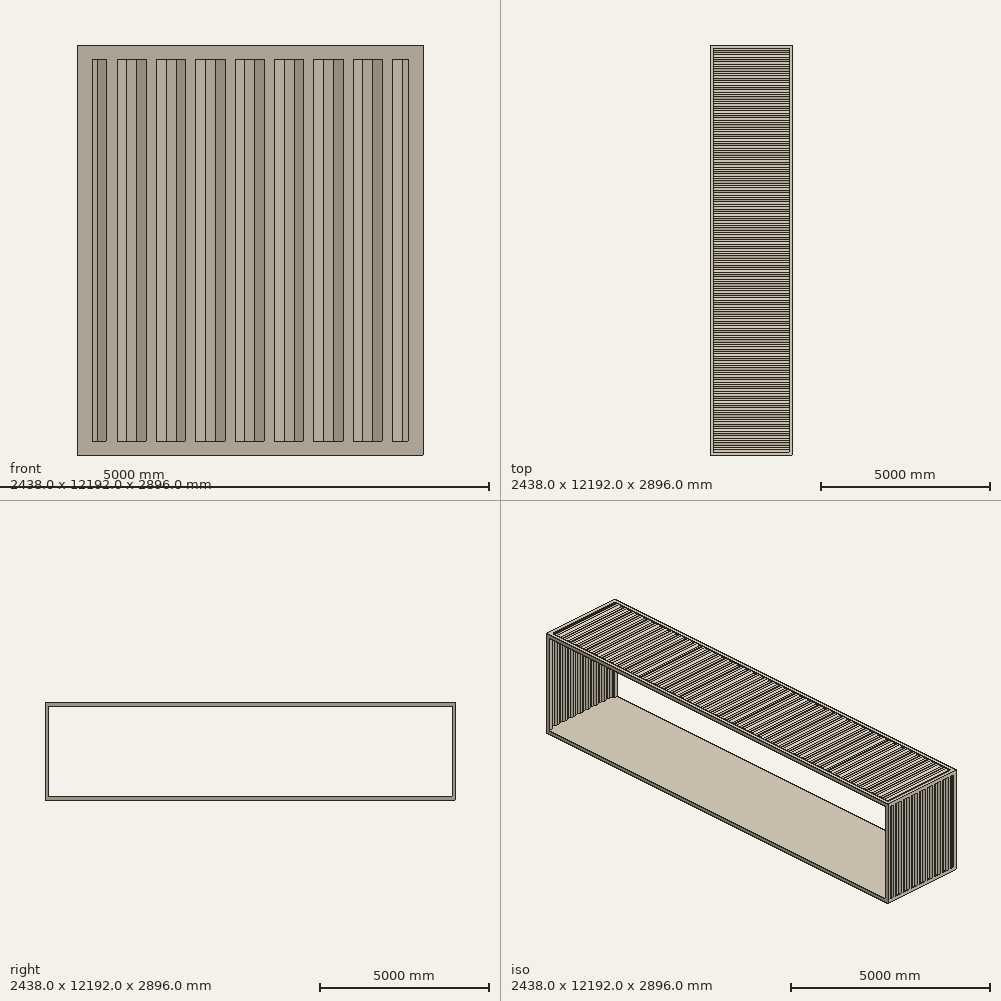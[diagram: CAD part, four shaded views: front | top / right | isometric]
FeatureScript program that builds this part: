
annotation { "Feature Type Name" : "Feature", "Feature Type Description" : "" }
export const myFeature = defineFeature(function(context is Context, id is Id, definition is map)
    precondition{}
    {
        {
            var Q0;
            Q0=qCreatedBy(makeId("Top.planeOp"),FACE);
            var sketch = newSketch(context, id + "F0", { "sketchPlane" : qUnion([Q0])});
            skLineSegment(sketch, "E0.bottom", {"start": v(0, 0) * mm, "end": v(-2438, 0) * mm});
            skLineSegment(sketch, "E0.top", {"start": v(0, 12192) * mm, "end": v(-2438, 12192) * mm});
            skLineSegment(sketch, "E0.left", {"start": v(0, 0) * mm, "end": v(0, 12192) * mm});
            skLineSegment(sketch, "E0.right", {"start": v(-2438, 0) * mm, "end": v(-2438, 12192) * mm});
            skSolve(sketch);
        }
        {
            var Q0;
            Q0=qSketchRegion(id+"F0",true);
            extrude(context, id + "F1", {"entities" : qUnion([Q0]), "depth" : 2896 * mm, "offsetDistance" : 25 * mm});
        }
        {
            var Q0;
            Q0=makeQuery(id+"F1.opExtrude","SWEPT_FACE",FACE,{"disambiguationData":[OSD([sQuery(id+"F0.wireOp",EDGE,"E0.bottom")])]});
            var sketch = newSketch(context, id + "F2", { "sketchPlane" : qUnion([Q0])});
            skLineSegment(sketch, "E1", {"start": v(-2438, 2896) * mm, "end": v(-2338, 2896) * mm});
            skLineSegment(sketch, "E2", {"start": v(-2338, 2896) * mm, "end": v(-2338, 100) * mm});
            skLineSegment(sketch, "E3", {"start": v(-2338, 100) * mm, "end": v(-100, 100) * mm});
            skLineSegment(sketch, "E4", {"start": v(-100, 100) * mm, "end": v(-100, 2796) * mm});
            skLineSegment(sketch, "E5", {"start": v(-100, 2796) * mm, "end": v(-2338, 2796) * mm});
            skSolve(sketch);
        }
        {
            var Q0;
            Q0=qSketchRegion(id+"F2",true);
            extrude(context, id + "F3", {"entities" : qUnion([Q0]), "operationType" : NewBodyOperationType.REMOVE, "oppositeDirection" : true, "depth" : 12192 * mm, "offsetDistance" : 25 * mm});
        }
        {
            var Q0;
            Q0=makeQuery(id+"F1.opExtrude","SWEPT_FACE",FACE,{"disambiguationData":[OSD([sQuery(id+"F0.wireOp",EDGE,"E0.left")])]});
            var sketch = newSketch(context, id + "F4", { "sketchPlane" : qUnion([Q0])});
            skLineSegment(sketch, "E6", {"start": v(0, 2896) * mm, "end": v(100, 2896) * mm});
            skLineSegment(sketch, "E7", {"start": v(100, 2896) * mm, "end": v(100, 100) * mm});
            skLineSegment(sketch, "E8", {"start": v(100, 100) * mm, "end": v(12092, 100) * mm});
            skLineSegment(sketch, "E9", {"start": v(12092, 100) * mm, "end": v(12092, 2796) * mm});
            skLineSegment(sketch, "E10", {"start": v(12092, 2796) * mm, "end": v(100, 2796) * mm});
            skSolve(sketch);
        }
        {
            var Q0;
            Q0=qSketchRegion(id+"F4",true);
            extrude(context, id + "F5", {"entities" : qUnion([Q0]), "operationType" : NewBodyOperationType.REMOVE, "oppositeDirection" : true, "depth" : 2438 * mm, "offsetDistance" : 25 * mm});
        }
        {
            var Q0;
            Q0=makeQuery(id+"F1.opExtrude","CAP_FACE",FACE,{"disambiguationData":[OSD([sQuery(id+"F0.wireOp",EDGE,"E0.bottom"),sQuery(id+"F0.wireOp",EDGE,"E0.top"),sQuery(id+"F0.wireOp",EDGE,"E0.left"),sQuery(id+"F0.wireOp",EDGE,"E0.right")])],"isStart":false});
            var sketch = newSketch(context, id + "F6", { "sketchPlane" : qUnion([Q0])});
            skLineSegment(sketch, "E11", {"start": v(-2438, 0) * mm, "end": v(-2338, 0) * mm});
            skLineSegment(sketch, "E12", {"start": v(-2338, 0) * mm, "end": v(-2338, 12092) * mm});
            skLineSegment(sketch, "E13", {"start": v(-2338, 12092) * mm, "end": v(-100, 12092) * mm});
            skLineSegment(sketch, "E14", {"start": v(-100, 12092) * mm, "end": v(-100, 100) * mm});
            skLineSegment(sketch, "E15", {"start": v(-100, 100) * mm, "end": v(-2338, 100) * mm});
            skSolve(sketch);
        }
        {
            var Q0;
            Q0=qSketchRegion(id+"F6",true);
            extrude(context, id + "F7", {"entities" : qUnion([Q0]), "operationType" : NewBodyOperationType.REMOVE, "oppositeDirection" : true, "depth" : 100 * mm, "offsetDistance" : 25 * mm});
        }
        {
            var Q0;
            Q0=makeQuery(id+"F5.boolean.opBoolean","MERGE",FACE,{"derivedFrom":[makeQuery(id+"F3.boolean.opBoolean","COPY",FACE,{"derivedFrom":makeQuery(id+"F3.opExtrude","SWEPT_FACE",FACE,{"disambiguationData":[OSD([sQuery(id+"F2.wireOp",EDGE,"E3")])]})})],"fromTools":[makeQuery(id+"F5.opExtrude","SWEPT_FACE",FACE,{"disambiguationData":[OSD([sQuery(id+"F4.wireOp",EDGE,"E8")])]})]});
            var sketch = newSketch(context, id + "F8", { "sketchPlane" : qUnion([Q0])});
            skLineSegment(sketch, "E16", {"start": v(-2338, 36) * mm, "end": v(-2301, 36) * mm});
            skLineSegment(sketch, "E17", {"start": v(-2233, 0) * mm, "end": v(-2161, 0) * mm});
            skLineSegment(sketch, "E18", {"start": v(-2093, 36) * mm, "end": v(-2023, 36) * mm});
            skLineSegment(sketch, "E19", {"start": v(-2301, 36) * mm, "end": v(-2233, 0) * mm});
            skLineSegment(sketch, "E20", {"start": v(-2161, 0) * mm, "end": v(-2093, 36) * mm});
            skLineSegment(sketch, "E21.1.0.0", {"start": v(-2023, 36) * mm, "end": v(-1955, 0) * mm});
            skLineSegment(sketch, "E21.1.0.1", {"start": v(-1955, 0) * mm, "end": v(-1883, 0) * mm});
            skLineSegment(sketch, "E21.1.0.2", {"start": v(-1883, 0) * mm, "end": v(-1815, 36) * mm});
            skLineSegment(sketch, "E21.1.0.3", {"start": v(-1815, 36) * mm, "end": v(-1745, 36) * mm});
            skLineSegment(sketch, "E21.2.0.0", {"start": v(-1745, 36) * mm, "end": v(-1677, 0) * mm});
            skLineSegment(sketch, "E21.2.0.1", {"start": v(-1677, 0) * mm, "end": v(-1605, 0) * mm});
            skLineSegment(sketch, "E21.2.0.2", {"start": v(-1605, 0) * mm, "end": v(-1537, 36) * mm});
            skLineSegment(sketch, "E21.2.0.3", {"start": v(-1537, 36) * mm, "end": v(-1467, 36) * mm});
            skLineSegment(sketch, "E21.3.0.0", {"start": v(-1467, 36) * mm, "end": v(-1399, 0) * mm});
            skLineSegment(sketch, "E21.3.0.1", {"start": v(-1399, 0) * mm, "end": v(-1327, 0) * mm});
            skLineSegment(sketch, "E21.3.0.2", {"start": v(-1327, 0) * mm, "end": v(-1259, 36) * mm});
            skLineSegment(sketch, "E21.3.0.3", {"start": v(-1259, 36) * mm, "end": v(-1189, 36) * mm});
            skLineSegment(sketch, "E21.4.0.0", {"start": v(-1189, 36) * mm, "end": v(-1121, 0) * mm});
            skLineSegment(sketch, "E21.4.0.1", {"start": v(-1121, 0) * mm, "end": v(-1049, 0) * mm});
            skLineSegment(sketch, "E21.4.0.2", {"start": v(-1049, 0) * mm, "end": v(-981, 36) * mm});
            skLineSegment(sketch, "E21.4.0.3", {"start": v(-981, 36) * mm, "end": v(-911, 36) * mm});
            skLineSegment(sketch, "E21.5.0.0", {"start": v(-911, 36) * mm, "end": v(-843, 0) * mm});
            skLineSegment(sketch, "E21.5.0.1", {"start": v(-843, 0) * mm, "end": v(-771, 0) * mm});
            skLineSegment(sketch, "E21.5.0.2", {"start": v(-771, 0) * mm, "end": v(-703, 36) * mm});
            skLineSegment(sketch, "E21.5.0.3", {"start": v(-703, 36) * mm, "end": v(-633, 36) * mm});
            skLineSegment(sketch, "E21.6.0.0", {"start": v(-633, 36) * mm, "end": v(-565, 0) * mm});
            skLineSegment(sketch, "E21.6.0.1", {"start": v(-565, 0) * mm, "end": v(-493, 0) * mm});
            skLineSegment(sketch, "E21.6.0.2", {"start": v(-493, 0) * mm, "end": v(-425, 36) * mm});
            skLineSegment(sketch, "E21.6.0.3", {"start": v(-425, 36) * mm, "end": v(-355, 36) * mm});
            skLineSegment(sketch, "E21.direction1", {"start": v(-2301, 36) * mm, "end": v(-2023, 36) * mm, "construction": true});
            skLineSegment(sketch, "E22.1.0.0", {"start": v(-355, 36) * mm, "end": v(-287, 0) * mm});
            skLineSegment(sketch, "E22.1.0.1", {"start": v(-287, 0) * mm, "end": v(-215, 0) * mm});
            skLineSegment(sketch, "E22.1.0.2", {"start": v(-215, 0) * mm, "end": v(-147, 36) * mm});
            skLineSegment(sketch, "E22.direction1", {"start": v(-633, 36) * mm, "end": v(-355, 36) * mm, "construction": true});
            skLineSegment(sketch, "E23", {"start": v(-147, 36) * mm, "end": v(-100, 36) * mm});
            skLineSegment(sketch, "E24.0.1.0", {"start": v(-2301, 37) * mm, "end": v(-2023, 37) * mm, "construction": true});
            skLineSegment(sketch, "E24.0.1.1", {"start": v(-633, 37) * mm, "end": v(-355, 37) * mm, "construction": true});
            skLineSegment(sketch, "E24.0.1.2", {"start": v(-355, 37) * mm, "end": v(-287, 1) * mm});
            skLineSegment(sketch, "E24.0.1.3", {"start": v(-1259, 37) * mm, "end": v(-1189, 37) * mm});
            skLineSegment(sketch, "E24.0.1.4", {"start": v(-147, 37) * mm, "end": v(-100, 37) * mm});
            skLineSegment(sketch, "E24.0.1.5", {"start": v(-1605, 1) * mm, "end": v(-1537, 37) * mm});
            skLineSegment(sketch, "E24.0.1.6", {"start": v(-1467, 37) * mm, "end": v(-1399, 1) * mm});
            skLineSegment(sketch, "E24.0.1.7", {"start": v(-1049, 1) * mm, "end": v(-981, 37) * mm});
            skLineSegment(sketch, "E24.0.1.8", {"start": v(-633, 37) * mm, "end": v(-565, 1) * mm});
            skLineSegment(sketch, "E24.0.1.9", {"start": v(-1955, 1) * mm, "end": v(-1883, 1) * mm});
            skLineSegment(sketch, "E24.0.1.10", {"start": v(-215, 1) * mm, "end": v(-147, 37) * mm});
            skLineSegment(sketch, "E24.0.1.11", {"start": v(-911, 37) * mm, "end": v(-843, 1) * mm});
            skLineSegment(sketch, "E24.0.1.12", {"start": v(-1883, 1) * mm, "end": v(-1815, 37) * mm});
            skLineSegment(sketch, "E24.0.1.13", {"start": v(-2023, 37) * mm, "end": v(-1955, 1) * mm});
            skLineSegment(sketch, "E24.0.1.14", {"start": v(-493, 1) * mm, "end": v(-425, 37) * mm});
            skLineSegment(sketch, "E24.0.1.15", {"start": v(-1677, 1) * mm, "end": v(-1605, 1) * mm});
            skLineSegment(sketch, "E24.0.1.16", {"start": v(-1189, 37) * mm, "end": v(-1121, 1) * mm});
            skLineSegment(sketch, "E24.0.1.17", {"start": v(-1745, 37) * mm, "end": v(-1677, 1) * mm});
            skLineSegment(sketch, "E24.0.1.18", {"start": v(-287, 1) * mm, "end": v(-215, 1) * mm});
            skLineSegment(sketch, "E24.0.1.19", {"start": v(-981, 37) * mm, "end": v(-911, 37) * mm});
            skLineSegment(sketch, "E24.0.1.20", {"start": v(-843, 1) * mm, "end": v(-771, 1) * mm});
            skLineSegment(sketch, "E24.0.1.21", {"start": v(-771, 1) * mm, "end": v(-703, 37) * mm});
            skLineSegment(sketch, "E24.0.1.22", {"start": v(-1815, 37) * mm, "end": v(-1745, 37) * mm});
            skLineSegment(sketch, "E24.0.1.23", {"start": v(-565, 1) * mm, "end": v(-493, 1) * mm});
            skLineSegment(sketch, "E24.0.1.24", {"start": v(-2161, 1) * mm, "end": v(-2093, 37) * mm});
            skLineSegment(sketch, "E24.0.1.25", {"start": v(-1121, 1) * mm, "end": v(-1049, 1) * mm});
            skLineSegment(sketch, "E24.0.1.26", {"start": v(-2301, 37) * mm, "end": v(-2233, 1) * mm});
            skLineSegment(sketch, "E24.0.1.27", {"start": v(-1537, 37) * mm, "end": v(-1467, 37) * mm});
            skLineSegment(sketch, "E24.0.1.28", {"start": v(-1399, 1) * mm, "end": v(-1327, 1) * mm});
            skLineSegment(sketch, "E24.0.1.29", {"start": v(-2233, 1) * mm, "end": v(-2161, 1) * mm});
            skLineSegment(sketch, "E24.0.1.30", {"start": v(-1327, 1) * mm, "end": v(-1259, 37) * mm});
            skLineSegment(sketch, "E24.0.1.31", {"start": v(-425, 37) * mm, "end": v(-355, 37) * mm});
            skLineSegment(sketch, "E24.0.1.32", {"start": v(-2093, 37) * mm, "end": v(-2023, 37) * mm});
            skLineSegment(sketch, "E24.0.1.33", {"start": v(-703, 37) * mm, "end": v(-633, 37) * mm});
            skLineSegment(sketch, "E24.0.1.34", {"start": v(-2338, 37) * mm, "end": v(-2301, 37) * mm});
            skLineSegment(sketch, "E24.direction1", {"start": v(-2338, 36) * mm, "end": v(-2313, 36) * mm, "construction": true});
            skLineSegment(sketch, "E24.direction2", {"start": v(-2338, 36) * mm, "end": v(-2338, 37) * mm, "construction": true});
            skLineSegment(sketch, "E25", {"start": v(-2338, 37) * mm, "end": v(-2338, 36) * mm});
            skLineSegment(sketch, "E26", {"start": v(-100, 37) * mm, "end": v(-100, 36) * mm});
            skSolve(sketch);
        }
        {
            var Q0;
            Q0=qSketchRegion(id+"F8",true);
            extrude(context, id + "F9", {"entities" : qUnion([Q0]), "operationType" : NewBodyOperationType.ADD, "depth" : 2696 * mm, "offsetDistance" : 25 * mm});
        }
        {
            var Q0;
            {var subQ4=makeQuery(id+"F3.boolean.opBoolean","COPY",FACE,{"derivedFrom":makeQuery(id+"F3.opExtrude","SWEPT_FACE",FACE,{"disambiguationData":[OSD([sQuery(id+"F2.wireOp",EDGE,"E3")])]})});var subQ5=makeQuery(id+"F5.opExtrude","SWEPT_FACE",FACE,{"disambiguationData":[OSD([sQuery(id+"F4.wireOp",EDGE,"E8")])]});Q0=makeQuery(id+"F9.boolean.opBoolean","SPLIT",FACE,{"disambiguationData":[TD([makeQuery(id+"F1.opExtrude","SWEPT_FACE",FACE,{"disambiguationData":[OSD([sQuery(id+"F0.wireOp",EDGE,"E0.top")])]})])],"derivedFrom":makeQuery(id+"F5.boolean.opBoolean","MERGE",FACE,{"derivedFrom":[subQ4],"fromTools":[subQ5]})});}
            var sketch = newSketch(context, id + "F10", { "sketchPlane" : qUnion([Q0])});
            skLineSegment(sketch, "E27", {"start": v(-100, 12156) * mm, "end": v(-137, 12156) * mm});
            skLineSegment(sketch, "E28", {"start": v(-205.08, 12191.96) * mm, "end": v(-277.08, 12191.96) * mm});
            skLineSegment(sketch, "E29", {"start": v(-345, 12156) * mm, "end": v(-415, 12156) * mm});
            skLineSegment(sketch, "E30", {"start": v(-137, 12156) * mm, "end": v(-205.08, 12191.96) * mm});
            skLineSegment(sketch, "E31", {"start": v(-277.08, 12191.96) * mm, "end": v(-345, 12156) * mm});
            skLineSegment(sketch, "E32.1.0.0", {"start": v(-415, 12156) * mm, "end": v(-483.08, 12191.96) * mm});
            skLineSegment(sketch, "E32.1.0.1", {"start": v(-483.08, 12191.96) * mm, "end": v(-555.08, 12191.96) * mm});
            skLineSegment(sketch, "E32.1.0.2", {"start": v(-555.08, 12191.96) * mm, "end": v(-623, 12156) * mm});
            skLineSegment(sketch, "E32.1.0.3", {"start": v(-623, 12156) * mm, "end": v(-693, 12156) * mm});
            skLineSegment(sketch, "E32.2.0.0", {"start": v(-693, 12156) * mm, "end": v(-761.08, 12191.96) * mm});
            skLineSegment(sketch, "E32.2.0.1", {"start": v(-761.08, 12191.96) * mm, "end": v(-833.08, 12191.96) * mm});
            skLineSegment(sketch, "E32.2.0.2", {"start": v(-833.08, 12191.96) * mm, "end": v(-901, 12156) * mm});
            skLineSegment(sketch, "E32.2.0.3", {"start": v(-901, 12156) * mm, "end": v(-971, 12156) * mm});
            skLineSegment(sketch, "E32.3.0.0", {"start": v(-971, 12156) * mm, "end": v(-1039.08, 12191.96) * mm});
            skLineSegment(sketch, "E32.3.0.1", {"start": v(-1039.08, 12191.96) * mm, "end": v(-1111.08, 12191.96) * mm});
            skLineSegment(sketch, "E32.3.0.2", {"start": v(-1111.08, 12191.96) * mm, "end": v(-1179, 12156) * mm});
            skLineSegment(sketch, "E32.3.0.3", {"start": v(-1179, 12156) * mm, "end": v(-1249, 12156) * mm});
            skLineSegment(sketch, "E32.4.0.0", {"start": v(-1249, 12156) * mm, "end": v(-1317.08, 12191.96) * mm});
            skLineSegment(sketch, "E32.4.0.1", {"start": v(-1317.08, 12191.96) * mm, "end": v(-1389.08, 12191.96) * mm});
            skLineSegment(sketch, "E32.4.0.2", {"start": v(-1389.08, 12191.96) * mm, "end": v(-1457, 12156) * mm});
            skLineSegment(sketch, "E32.4.0.3", {"start": v(-1457, 12156) * mm, "end": v(-1527, 12156) * mm});
            skLineSegment(sketch, "E32.5.0.0", {"start": v(-1527, 12156) * mm, "end": v(-1595.08, 12191.96) * mm});
            skLineSegment(sketch, "E32.5.0.1", {"start": v(-1595.08, 12191.96) * mm, "end": v(-1667.08, 12191.96) * mm});
            skLineSegment(sketch, "E32.5.0.2", {"start": v(-1667.08, 12191.96) * mm, "end": v(-1735, 12156) * mm});
            skLineSegment(sketch, "E32.5.0.3", {"start": v(-1735, 12156) * mm, "end": v(-1805, 12156) * mm});
            skLineSegment(sketch, "E32.6.0.0", {"start": v(-1805, 12156) * mm, "end": v(-1873.08, 12191.96) * mm});
            skLineSegment(sketch, "E32.6.0.1", {"start": v(-1873.08, 12191.96) * mm, "end": v(-1945.08, 12191.96) * mm});
            skLineSegment(sketch, "E32.6.0.2", {"start": v(-1945.08, 12191.96) * mm, "end": v(-2013, 12156) * mm});
            skLineSegment(sketch, "E32.6.0.3", {"start": v(-2013, 12156) * mm, "end": v(-2083, 12156) * mm});
            skLineSegment(sketch, "E32.direction1", {"start": v(-137, 12156) * mm, "end": v(-415, 12156) * mm, "construction": true});
            skLineSegment(sketch, "E33.1.0.0", {"start": v(-2083, 12156) * mm, "end": v(-2151.08, 12191.96) * mm});
            skLineSegment(sketch, "E33.1.0.1", {"start": v(-2151.08, 12191.96) * mm, "end": v(-2223.08, 12191.96) * mm});
            skLineSegment(sketch, "E33.1.0.2", {"start": v(-2223.08, 12191.96) * mm, "end": v(-2291, 12156) * mm});
            skLineSegment(sketch, "E33.direction1", {"start": v(-1805, 12156) * mm, "end": v(-2083, 12156) * mm, "construction": true});
            skLineSegment(sketch, "E34", {"start": v(-2291, 12156) * mm, "end": v(-2338, 12156) * mm});
            skLineSegment(sketch, "E35.0.1.0", {"start": v(-137, 12155) * mm, "end": v(-415, 12155) * mm, "construction": true});
            skLineSegment(sketch, "E35.0.1.1", {"start": v(-1805, 12155) * mm, "end": v(-2083, 12155) * mm, "construction": true});
            skLineSegment(sketch, "E35.0.1.2", {"start": v(-2083, 12155) * mm, "end": v(-2151.08, 12190.96) * mm});
            skLineSegment(sketch, "E35.0.1.3", {"start": v(-1179, 12155) * mm, "end": v(-1249, 12155) * mm});
            skLineSegment(sketch, "E35.0.1.4", {"start": v(-2291, 12155) * mm, "end": v(-2338, 12155) * mm});
            skLineSegment(sketch, "E35.0.1.5", {"start": v(-833.08, 12190.96) * mm, "end": v(-901, 12155) * mm});
            skLineSegment(sketch, "E35.0.1.6", {"start": v(-971, 12155) * mm, "end": v(-1039.08, 12190.96) * mm});
            skLineSegment(sketch, "E35.0.1.7", {"start": v(-1389.08, 12190.96) * mm, "end": v(-1457, 12155) * mm});
            skLineSegment(sketch, "E35.0.1.8", {"start": v(-1805, 12155) * mm, "end": v(-1873.08, 12190.96) * mm});
            skLineSegment(sketch, "E35.0.1.9", {"start": v(-483.08, 12190.96) * mm, "end": v(-555.08, 12190.96) * mm});
            skLineSegment(sketch, "E35.0.1.10", {"start": v(-2223.08, 12190.96) * mm, "end": v(-2291, 12155) * mm});
            skLineSegment(sketch, "E35.0.1.11", {"start": v(-1527, 12155) * mm, "end": v(-1595.08, 12190.96) * mm});
            skLineSegment(sketch, "E35.0.1.12", {"start": v(-555.08, 12190.96) * mm, "end": v(-623, 12155) * mm});
            skLineSegment(sketch, "E35.0.1.13", {"start": v(-415, 12155) * mm, "end": v(-483.08, 12190.96) * mm});
            skLineSegment(sketch, "E35.0.1.14", {"start": v(-1945.08, 12190.96) * mm, "end": v(-2013, 12155) * mm});
            skLineSegment(sketch, "E35.0.1.15", {"start": v(-761.08, 12190.96) * mm, "end": v(-833.08, 12190.96) * mm});
            skLineSegment(sketch, "E35.0.1.16", {"start": v(-1249, 12155) * mm, "end": v(-1317.08, 12190.96) * mm});
            skLineSegment(sketch, "E35.0.1.17", {"start": v(-693, 12155) * mm, "end": v(-761.08, 12190.96) * mm});
            skLineSegment(sketch, "E35.0.1.18", {"start": v(-2151.08, 12190.96) * mm, "end": v(-2223.08, 12190.96) * mm});
            skLineSegment(sketch, "E35.0.1.19", {"start": v(-1457, 12155) * mm, "end": v(-1527, 12155) * mm});
            skLineSegment(sketch, "E35.0.1.20", {"start": v(-1595.08, 12190.96) * mm, "end": v(-1667.08, 12190.96) * mm});
            skLineSegment(sketch, "E35.0.1.21", {"start": v(-1667.08, 12190.96) * mm, "end": v(-1735, 12155) * mm});
            skLineSegment(sketch, "E35.0.1.22", {"start": v(-623, 12155) * mm, "end": v(-693, 12155) * mm});
            skLineSegment(sketch, "E35.0.1.23", {"start": v(-1873.08, 12190.96) * mm, "end": v(-1945.08, 12190.96) * mm});
            skLineSegment(sketch, "E35.0.1.24", {"start": v(-277.08, 12190.96) * mm, "end": v(-345, 12155) * mm});
            skLineSegment(sketch, "E35.0.1.25", {"start": v(-1317.08, 12190.96) * mm, "end": v(-1389.08, 12190.96) * mm});
            skLineSegment(sketch, "E35.0.1.26", {"start": v(-137, 12155) * mm, "end": v(-205.08, 12190.96) * mm});
            skLineSegment(sketch, "E35.0.1.27", {"start": v(-901, 12155) * mm, "end": v(-971, 12155) * mm});
            skLineSegment(sketch, "E35.0.1.28", {"start": v(-1039.08, 12190.96) * mm, "end": v(-1111.08, 12190.96) * mm});
            skLineSegment(sketch, "E35.0.1.29", {"start": v(-205.08, 12190.96) * mm, "end": v(-277.08, 12190.96) * mm});
            skLineSegment(sketch, "E35.0.1.30", {"start": v(-1111.08, 12190.96) * mm, "end": v(-1179, 12155) * mm});
            skLineSegment(sketch, "E35.0.1.31", {"start": v(-2013, 12155) * mm, "end": v(-2083, 12155) * mm});
            skLineSegment(sketch, "E35.0.1.32", {"start": v(-345, 12155) * mm, "end": v(-415, 12155) * mm});
            skLineSegment(sketch, "E35.0.1.33", {"start": v(-1735, 12155) * mm, "end": v(-1805, 12155) * mm});
            skLineSegment(sketch, "E35.0.1.34", {"start": v(-100, 12155) * mm, "end": v(-137, 12155) * mm});
            skLineSegment(sketch, "E35.direction1", {"start": v(-100, 12156) * mm, "end": v(-125, 12156) * mm, "construction": true});
            skLineSegment(sketch, "E35.direction2", {"start": v(-100, 12156) * mm, "end": v(-100, 12155) * mm, "construction": true});
            skLineSegment(sketch, "E36", {"start": v(-100, 12156) * mm, "end": v(-100, 12155) * mm});
            skLineSegment(sketch, "E37", {"start": v(-2338, 12156) * mm, "end": v(-2338, 12155) * mm});
            skSolve(sketch);
        }
        {
            var Q0;
            Q0=qSketchRegion(id+"F10",true);
            extrude(context, id + "F11", {"entities" : qUnion([Q0]), "operationType" : NewBodyOperationType.ADD, "depth" : 2696 * mm, "offsetDistance" : 25 * mm});
        }
        {
            var Q0;
            Q0=makeQuery(id+"F7.boolean.opBoolean","COPY",FACE,{"derivedFrom":makeQuery(id+"F7.opExtrude","SWEPT_FACE",FACE,{"disambiguationData":[OSD([sQuery(id+"F6.wireOp",EDGE,"E12")])]})});
            var sketch = newSketch(context, id + "F12", { "sketchPlane" : qUnion([Q0])});
            skLineSegment(sketch, "E38", {"start": v(12091.83, 2859.97) * mm, "end": v(12054.83, 2859.97) * mm});
            skLineSegment(sketch, "E39", {"start": v(11986.83, 2895.97) * mm, "end": v(11914.83, 2895.97) * mm});
            skLineSegment(sketch, "E40", {"start": v(11846.83, 2859.97) * mm, "end": v(11776.83, 2859.97) * mm});
            skLineSegment(sketch, "E41", {"start": v(12054.83, 2859.97) * mm, "end": v(11986.83, 2895.97) * mm});
            skLineSegment(sketch, "E42", {"start": v(11914.83, 2895.97) * mm, "end": v(11846.83, 2859.97) * mm});
            skLineSegment(sketch, "E43.1.0.0", {"start": v(11776.83, 2859.97) * mm, "end": v(11708.83, 2895.97) * mm});
            skLineSegment(sketch, "E43.1.0.1", {"start": v(11708.83, 2895.97) * mm, "end": v(11636.83, 2895.97) * mm});
            skLineSegment(sketch, "E43.1.0.2", {"start": v(11636.83, 2895.97) * mm, "end": v(11568.83, 2859.97) * mm});
            skLineSegment(sketch, "E43.1.0.3", {"start": v(11568.83, 2859.97) * mm, "end": v(11498.83, 2859.97) * mm});
            skLineSegment(sketch, "E43.2.0.0", {"start": v(11498.83, 2859.97) * mm, "end": v(11430.83, 2895.97) * mm});
            skLineSegment(sketch, "E43.2.0.1", {"start": v(11430.83, 2895.97) * mm, "end": v(11358.83, 2895.97) * mm});
            skLineSegment(sketch, "E43.2.0.2", {"start": v(11358.83, 2895.97) * mm, "end": v(11290.83, 2859.97) * mm});
            skLineSegment(sketch, "E43.2.0.3", {"start": v(11290.83, 2859.97) * mm, "end": v(11220.83, 2859.97) * mm});
            skLineSegment(sketch, "E43.3.0.0", {"start": v(11220.83, 2859.97) * mm, "end": v(11152.83, 2895.97) * mm});
            skLineSegment(sketch, "E43.3.0.1", {"start": v(11152.83, 2895.97) * mm, "end": v(11080.83, 2895.97) * mm});
            skLineSegment(sketch, "E43.3.0.2", {"start": v(11080.83, 2895.97) * mm, "end": v(11012.83, 2859.97) * mm});
            skLineSegment(sketch, "E43.3.0.3", {"start": v(11012.83, 2859.97) * mm, "end": v(10942.83, 2859.97) * mm});
            skLineSegment(sketch, "E43.4.0.0", {"start": v(10942.83, 2859.97) * mm, "end": v(10874.83, 2895.97) * mm});
            skLineSegment(sketch, "E43.4.0.1", {"start": v(10874.83, 2895.97) * mm, "end": v(10802.83, 2895.97) * mm});
            skLineSegment(sketch, "E43.4.0.2", {"start": v(10802.83, 2895.97) * mm, "end": v(10734.83, 2859.97) * mm});
            skLineSegment(sketch, "E43.4.0.3", {"start": v(10734.83, 2859.97) * mm, "end": v(10664.83, 2859.97) * mm});
            skLineSegment(sketch, "E43.5.0.0", {"start": v(10664.83, 2859.97) * mm, "end": v(10596.83, 2895.97) * mm});
            skLineSegment(sketch, "E43.5.0.1", {"start": v(10596.83, 2895.97) * mm, "end": v(10524.83, 2895.97) * mm});
            skLineSegment(sketch, "E43.5.0.2", {"start": v(10524.83, 2895.97) * mm, "end": v(10456.83, 2859.97) * mm});
            skLineSegment(sketch, "E43.5.0.3", {"start": v(10456.83, 2859.97) * mm, "end": v(10386.83, 2859.97) * mm});
            skLineSegment(sketch, "E43.6.0.0", {"start": v(10386.83, 2859.97) * mm, "end": v(10318.83, 2895.97) * mm});
            skLineSegment(sketch, "E43.6.0.1", {"start": v(10318.83, 2895.97) * mm, "end": v(10246.83, 2895.97) * mm});
            skLineSegment(sketch, "E43.6.0.2", {"start": v(10246.83, 2895.97) * mm, "end": v(10178.83, 2859.97) * mm});
            skLineSegment(sketch, "E43.6.0.3", {"start": v(10178.83, 2859.97) * mm, "end": v(10108.83, 2859.97) * mm});
            skLineSegment(sketch, "E43.direction1", {"start": v(12054.83, 2859.97) * mm, "end": v(11776.83, 2859.97) * mm, "construction": true});
            skLineSegment(sketch, "E44.1.0.0", {"start": v(10108.83, 2859.97) * mm, "end": v(10040.83, 2895.97) * mm});
            skLineSegment(sketch, "E44.1.0.1", {"start": v(10040.83, 2895.97) * mm, "end": v(9968.83, 2895.97) * mm});
            skLineSegment(sketch, "E44.1.0.2", {"start": v(9968.83, 2895.97) * mm, "end": v(9900.83, 2859.97) * mm});
            skLineSegment(sketch, "E44.direction1", {"start": v(10386.83, 2859.97) * mm, "end": v(10108.83, 2859.97) * mm, "construction": true});
            skLineSegment(sketch, "E45.0.1.0", {"start": v(12054.83, 2858.97) * mm, "end": v(11776.83, 2858.97) * mm, "construction": true});
            skLineSegment(sketch, "E45.0.1.1", {"start": v(10386.83, 2858.97) * mm, "end": v(10108.83, 2858.97) * mm, "construction": true});
            skLineSegment(sketch, "E45.0.1.2", {"start": v(10108.83, 2858.97) * mm, "end": v(10040.83, 2894.97) * mm});
            skLineSegment(sketch, "E45.0.1.3", {"start": v(11012.83, 2858.97) * mm, "end": v(10942.83, 2858.97) * mm});
            skLineSegment(sketch, "E45.0.1.5", {"start": v(11358.83, 2894.97) * mm, "end": v(11290.83, 2858.97) * mm});
            skLineSegment(sketch, "E45.0.1.6", {"start": v(11220.83, 2858.97) * mm, "end": v(11152.83, 2894.97) * mm});
            skLineSegment(sketch, "E45.0.1.7", {"start": v(10802.83, 2894.97) * mm, "end": v(10734.83, 2858.97) * mm});
            skLineSegment(sketch, "E45.0.1.8", {"start": v(10386.83, 2858.97) * mm, "end": v(10318.83, 2894.97) * mm});
            skLineSegment(sketch, "E45.0.1.9", {"start": v(11708.83, 2894.97) * mm, "end": v(11636.83, 2894.97) * mm});
            skLineSegment(sketch, "E45.0.1.10", {"start": v(9968.83, 2894.97) * mm, "end": v(9900.83, 2858.97) * mm});
            skLineSegment(sketch, "E45.0.1.11", {"start": v(10664.83, 2858.97) * mm, "end": v(10596.83, 2894.97) * mm});
            skLineSegment(sketch, "E45.0.1.12", {"start": v(11636.83, 2894.97) * mm, "end": v(11568.83, 2858.97) * mm});
            skLineSegment(sketch, "E45.0.1.13", {"start": v(11776.83, 2858.97) * mm, "end": v(11708.83, 2894.97) * mm});
            skLineSegment(sketch, "E45.0.1.14", {"start": v(10246.83, 2894.97) * mm, "end": v(10178.83, 2858.97) * mm});
            skLineSegment(sketch, "E45.0.1.15", {"start": v(11430.83, 2894.97) * mm, "end": v(11358.83, 2894.97) * mm});
            skLineSegment(sketch, "E45.0.1.16", {"start": v(10942.83, 2858.97) * mm, "end": v(10874.83, 2894.97) * mm});
            skLineSegment(sketch, "E45.0.1.17", {"start": v(11498.83, 2858.97) * mm, "end": v(11430.83, 2894.97) * mm});
            skLineSegment(sketch, "E45.0.1.18", {"start": v(10040.83, 2894.97) * mm, "end": v(9968.83, 2894.97) * mm});
            skLineSegment(sketch, "E45.0.1.19", {"start": v(10734.83, 2858.97) * mm, "end": v(10664.83, 2858.97) * mm});
            skLineSegment(sketch, "E45.0.1.20", {"start": v(10596.83, 2894.97) * mm, "end": v(10524.83, 2894.97) * mm});
            skLineSegment(sketch, "E45.0.1.21", {"start": v(10524.83, 2894.97) * mm, "end": v(10456.83, 2858.97) * mm});
            skLineSegment(sketch, "E45.0.1.22", {"start": v(11568.83, 2858.97) * mm, "end": v(11498.83, 2858.97) * mm});
            skLineSegment(sketch, "E45.0.1.23", {"start": v(10318.83, 2894.97) * mm, "end": v(10246.83, 2894.97) * mm});
            skLineSegment(sketch, "E45.0.1.24", {"start": v(11914.83, 2894.97) * mm, "end": v(11846.83, 2858.97) * mm});
            skLineSegment(sketch, "E45.0.1.25", {"start": v(10874.83, 2894.97) * mm, "end": v(10802.83, 2894.97) * mm});
            skLineSegment(sketch, "E45.0.1.26", {"start": v(12054.83, 2858.97) * mm, "end": v(11986.83, 2894.97) * mm});
            skLineSegment(sketch, "E45.0.1.27", {"start": v(11290.83, 2858.97) * mm, "end": v(11220.83, 2858.97) * mm});
            skLineSegment(sketch, "E45.0.1.28", {"start": v(11152.83, 2894.97) * mm, "end": v(11080.83, 2894.97) * mm});
            skLineSegment(sketch, "E45.0.1.29", {"start": v(11986.83, 2894.97) * mm, "end": v(11914.83, 2894.97) * mm});
            skLineSegment(sketch, "E45.0.1.30", {"start": v(11080.83, 2894.97) * mm, "end": v(11012.83, 2858.97) * mm});
            skLineSegment(sketch, "E45.0.1.31", {"start": v(10178.83, 2858.97) * mm, "end": v(10108.83, 2858.97) * mm});
            skLineSegment(sketch, "E45.0.1.32", {"start": v(11846.83, 2858.97) * mm, "end": v(11776.83, 2858.97) * mm});
            skLineSegment(sketch, "E45.0.1.33", {"start": v(10456.83, 2858.97) * mm, "end": v(10386.83, 2858.97) * mm});
            skLineSegment(sketch, "E45.0.1.34", {"start": v(12091.83, 2858.97) * mm, "end": v(12054.83, 2858.97) * mm});
            skLineSegment(sketch, "E46", {"start": v(12091.83, 2858.97) * mm, "end": v(12092, 2858.97) * mm});
            skLineSegment(sketch, "E47", {"start": v(12092, 2858.97) * mm, "end": v(12092, 2859.97) * mm});
            skLineSegment(sketch, "E48", {"start": v(12092, 2859.97) * mm, "end": v(12091.83, 2859.97) * mm});
            skLineSegment(sketch, "E49.0.1.0", {"start": v(9412.83, 2895.97) * mm, "end": v(9344.83, 2859.97) * mm});
            skLineSegment(sketch, "E49.0.1.1", {"start": v(9412.83, 2894.97) * mm, "end": v(9344.83, 2858.97) * mm});
            skLineSegment(sketch, "E49.0.1.2", {"start": v(9484.83, 2895.97) * mm, "end": v(9412.83, 2895.97) * mm});
            skLineSegment(sketch, "E49.0.1.3", {"start": v(9762.83, 2895.97) * mm, "end": v(9690.83, 2895.97) * mm});
            skLineSegment(sketch, "E49.0.1.4", {"start": v(9552.83, 2858.97) * mm, "end": v(9484.83, 2894.97) * mm});
            skLineSegment(sketch, "E49.0.1.5", {"start": v(9622.83, 2858.97) * mm, "end": v(9552.83, 2858.97) * mm});
            skLineSegment(sketch, "E49.0.1.6", {"start": v(9274.83, 2858.97) * mm, "end": v(9206.83, 2894.97) * mm});
            skLineSegment(sketch, "E49.0.1.7", {"start": v(9690.83, 2894.97) * mm, "end": v(9622.83, 2858.97) * mm});
            skLineSegment(sketch, "E49.0.1.8", {"start": v(9274.83, 2859.97) * mm, "end": v(9206.83, 2895.97) * mm});
            skLineSegment(sketch, "E49.0.1.9", {"start": v(9622.83, 2859.97) * mm, "end": v(9552.83, 2859.97) * mm});
            skLineSegment(sketch, "E49.0.1.10", {"start": v(9900.83, 2858.97) * mm, "end": v(9830.83, 2858.97) * mm});
            skLineSegment(sketch, "E49.0.1.11", {"start": v(9344.83, 2859.97) * mm, "end": v(9274.83, 2859.97) * mm});
            skLineSegment(sketch, "E49.0.1.12", {"start": v(9484.83, 2894.97) * mm, "end": v(9412.83, 2894.97) * mm});
            skLineSegment(sketch, "E49.0.1.13", {"start": v(9830.83, 2858.97) * mm, "end": v(9762.83, 2894.97) * mm});
            skLineSegment(sketch, "E49.0.1.14", {"start": v(9830.83, 2859.97) * mm, "end": v(9762.83, 2895.97) * mm});
            skLineSegment(sketch, "E49.0.1.15", {"start": v(9206.83, 2895.97) * mm, "end": v(9134.83, 2895.97) * mm});
            skLineSegment(sketch, "E49.0.1.16", {"start": v(9690.83, 2895.97) * mm, "end": v(9622.83, 2859.97) * mm});
            skLineSegment(sketch, "E49.0.1.17", {"start": v(9900.83, 2859.97) * mm, "end": v(9830.83, 2859.97) * mm});
            skLineSegment(sketch, "E49.0.1.18", {"start": v(9762.83, 2894.97) * mm, "end": v(9690.83, 2894.97) * mm});
            skLineSegment(sketch, "E49.0.1.19", {"start": v(9552.83, 2859.97) * mm, "end": v(9484.83, 2895.97) * mm});
            skLineSegment(sketch, "E49.0.1.20", {"start": v(9206.83, 2894.97) * mm, "end": v(9134.83, 2894.97) * mm});
            skLineSegment(sketch, "E49.0.1.21", {"start": v(9344.83, 2858.97) * mm, "end": v(9274.83, 2858.97) * mm});
            skLineSegment(sketch, "E49.0.1.22", {"start": v(8440.83, 2859.97) * mm, "end": v(8162.83, 2859.97) * mm, "construction": true});
            skLineSegment(sketch, "E49.0.1.23", {"start": v(8022.83, 2895.97) * mm, "end": v(7954.83, 2859.97) * mm});
            skLineSegment(sketch, "E49.0.1.24", {"start": v(8022.83, 2894.97) * mm, "end": v(7954.83, 2858.97) * mm});
            skLineSegment(sketch, "E49.0.1.25", {"start": v(8440.83, 2858.97) * mm, "end": v(8162.83, 2858.97) * mm, "construction": true});
            skLineSegment(sketch, "E49.0.1.26", {"start": v(8856.83, 2894.97) * mm, "end": v(8788.83, 2858.97) * mm});
            skLineSegment(sketch, "E49.0.1.27", {"start": v(8856.83, 2895.97) * mm, "end": v(8788.83, 2859.97) * mm});
            skLineSegment(sketch, "E49.0.1.28", {"start": v(8094.83, 2895.97) * mm, "end": v(8022.83, 2895.97) * mm});
            skLineSegment(sketch, "E49.0.1.29", {"start": v(8162.83, 2859.97) * mm, "end": v(8094.83, 2895.97) * mm});
            skLineSegment(sketch, "E49.0.1.30", {"start": v(8928.83, 2895.97) * mm, "end": v(8856.83, 2895.97) * mm});
            skLineSegment(sketch, "E49.0.1.31", {"start": v(8928.83, 2894.97) * mm, "end": v(8856.83, 2894.97) * mm});
            skLineSegment(sketch, "E49.0.1.32", {"start": v(8162.83, 2858.97) * mm, "end": v(8094.83, 2894.97) * mm});
            skLineSegment(sketch, "E49.0.1.33", {"start": v(8094.83, 2894.97) * mm, "end": v(8022.83, 2894.97) * mm});
            skLineSegment(sketch, "E49.0.1.34", {"start": v(8510.83, 2858.97) * mm, "end": v(8440.83, 2858.97) * mm});
            skLineSegment(sketch, "E49.0.1.35", {"start": v(8650.83, 2894.97) * mm, "end": v(8578.83, 2894.97) * mm});
            skLineSegment(sketch, "E49.0.1.36", {"start": v(9066.83, 2858.97) * mm, "end": v(8996.83, 2858.97) * mm});
            skLineSegment(sketch, "E49.0.1.37", {"start": v(8300.83, 2894.97) * mm, "end": v(8232.83, 2858.97) * mm});
            skLineSegment(sketch, "E49.0.1.38", {"start": v(8718.83, 2859.97) * mm, "end": v(8650.83, 2895.97) * mm});
            skLineSegment(sketch, "E49.0.1.39", {"start": v(8578.83, 2894.97) * mm, "end": v(8510.83, 2858.97) * mm});
            skLineSegment(sketch, "E49.0.1.40", {"start": v(8372.83, 2895.97) * mm, "end": v(8300.83, 2895.97) * mm});
            skLineSegment(sketch, "E49.0.1.41", {"start": v(8440.83, 2859.97) * mm, "end": v(8372.83, 2895.97) * mm});
            skLineSegment(sketch, "E49.0.1.42", {"start": v(8650.83, 2895.97) * mm, "end": v(8578.83, 2895.97) * mm});
            skLineSegment(sketch, "E49.0.1.43", {"start": v(9066.83, 2859.97) * mm, "end": v(8996.83, 2859.97) * mm});
            skLineSegment(sketch, "E49.0.1.44", {"start": v(8718.83, 2858.97) * mm, "end": v(8650.83, 2894.97) * mm});
            skLineSegment(sketch, "E49.0.1.45", {"start": v(8996.83, 2858.97) * mm, "end": v(8928.83, 2894.97) * mm});
            skLineSegment(sketch, "E49.0.1.46", {"start": v(9134.83, 2894.97) * mm, "end": v(9066.83, 2858.97) * mm});
            skLineSegment(sketch, "E49.0.1.47", {"start": v(8372.83, 2894.97) * mm, "end": v(8300.83, 2894.97) * mm});
            skLineSegment(sketch, "E49.0.1.48", {"start": v(8788.83, 2858.97) * mm, "end": v(8718.83, 2858.97) * mm});
            skLineSegment(sketch, "E49.0.1.49", {"start": v(8232.83, 2858.97) * mm, "end": v(8162.83, 2858.97) * mm});
            skLineSegment(sketch, "E49.0.1.50", {"start": v(8788.83, 2859.97) * mm, "end": v(8718.83, 2859.97) * mm});
            skLineSegment(sketch, "E49.0.1.51", {"start": v(9134.83, 2895.97) * mm, "end": v(9066.83, 2859.97) * mm});
            skLineSegment(sketch, "E49.0.1.52", {"start": v(8996.83, 2859.97) * mm, "end": v(8928.83, 2895.97) * mm});
            skLineSegment(sketch, "E49.0.1.53", {"start": v(8232.83, 2859.97) * mm, "end": v(8162.83, 2859.97) * mm});
            skLineSegment(sketch, "E49.0.1.54", {"start": v(8510.83, 2859.97) * mm, "end": v(8440.83, 2859.97) * mm});
            skLineSegment(sketch, "E49.0.1.55", {"start": v(8300.83, 2895.97) * mm, "end": v(8232.83, 2859.97) * mm});
            skLineSegment(sketch, "E49.0.1.56", {"start": v(8578.83, 2895.97) * mm, "end": v(8510.83, 2859.97) * mm});
            skLineSegment(sketch, "E49.0.1.57", {"start": v(8440.83, 2858.97) * mm, "end": v(8372.83, 2894.97) * mm});
            skLineSegment(sketch, "E49.0.2.0", {"start": v(7466.83, 2895.97) * mm, "end": v(7398.83, 2859.97) * mm});
            skLineSegment(sketch, "E49.0.2.1", {"start": v(7466.83, 2894.97) * mm, "end": v(7398.83, 2858.97) * mm});
            skLineSegment(sketch, "E49.0.2.2", {"start": v(7538.83, 2895.97) * mm, "end": v(7466.83, 2895.97) * mm});
            skLineSegment(sketch, "E49.0.2.3", {"start": v(7816.83, 2895.97) * mm, "end": v(7744.83, 2895.97) * mm});
            skLineSegment(sketch, "E49.0.2.4", {"start": v(7606.83, 2858.97) * mm, "end": v(7538.83, 2894.97) * mm});
            skLineSegment(sketch, "E49.0.2.5", {"start": v(7676.83, 2858.97) * mm, "end": v(7606.83, 2858.97) * mm});
            skLineSegment(sketch, "E49.0.2.6", {"start": v(7328.83, 2858.97) * mm, "end": v(7260.83, 2894.97) * mm});
            skLineSegment(sketch, "E49.0.2.7", {"start": v(7744.83, 2894.97) * mm, "end": v(7676.83, 2858.97) * mm});
            skLineSegment(sketch, "E49.0.2.8", {"start": v(7328.83, 2859.97) * mm, "end": v(7260.83, 2895.97) * mm});
            skLineSegment(sketch, "E49.0.2.9", {"start": v(7676.83, 2859.97) * mm, "end": v(7606.83, 2859.97) * mm});
            skLineSegment(sketch, "E49.0.2.10", {"start": v(7954.83, 2858.97) * mm, "end": v(7884.83, 2858.97) * mm});
            skLineSegment(sketch, "E49.0.2.11", {"start": v(7398.83, 2859.97) * mm, "end": v(7328.83, 2859.97) * mm});
            skLineSegment(sketch, "E49.0.2.12", {"start": v(7538.83, 2894.97) * mm, "end": v(7466.83, 2894.97) * mm});
            skLineSegment(sketch, "E49.0.2.13", {"start": v(7884.83, 2858.97) * mm, "end": v(7816.83, 2894.97) * mm});
            skLineSegment(sketch, "E49.0.2.14", {"start": v(7884.83, 2859.97) * mm, "end": v(7816.83, 2895.97) * mm});
            skLineSegment(sketch, "E49.0.2.15", {"start": v(7260.83, 2895.97) * mm, "end": v(7188.83, 2895.97) * mm});
            skLineSegment(sketch, "E49.0.2.16", {"start": v(7744.83, 2895.97) * mm, "end": v(7676.83, 2859.97) * mm});
            skLineSegment(sketch, "E49.0.2.17", {"start": v(7954.83, 2859.97) * mm, "end": v(7884.83, 2859.97) * mm});
            skLineSegment(sketch, "E49.0.2.18", {"start": v(7816.83, 2894.97) * mm, "end": v(7744.83, 2894.97) * mm});
            skLineSegment(sketch, "E49.0.2.19", {"start": v(7606.83, 2859.97) * mm, "end": v(7538.83, 2895.97) * mm});
            skLineSegment(sketch, "E49.0.2.20", {"start": v(7260.83, 2894.97) * mm, "end": v(7188.83, 2894.97) * mm});
            skLineSegment(sketch, "E49.0.2.21", {"start": v(7398.83, 2858.97) * mm, "end": v(7328.83, 2858.97) * mm});
            skLineSegment(sketch, "E49.0.2.22", {"start": v(6494.83, 2859.97) * mm, "end": v(6216.83, 2859.97) * mm, "construction": true});
            skLineSegment(sketch, "E49.0.2.23", {"start": v(6076.83, 2895.97) * mm, "end": v(6008.83, 2859.97) * mm});
            skLineSegment(sketch, "E49.0.2.24", {"start": v(6076.83, 2894.97) * mm, "end": v(6008.83, 2858.97) * mm});
            skLineSegment(sketch, "E49.0.2.25", {"start": v(6494.83, 2858.97) * mm, "end": v(6216.83, 2858.97) * mm, "construction": true});
            skLineSegment(sketch, "E49.0.2.26", {"start": v(6910.83, 2894.97) * mm, "end": v(6842.83, 2858.97) * mm});
            skLineSegment(sketch, "E49.0.2.27", {"start": v(6910.83, 2895.97) * mm, "end": v(6842.83, 2859.97) * mm});
            skLineSegment(sketch, "E49.0.2.28", {"start": v(6148.83, 2895.97) * mm, "end": v(6076.83, 2895.97) * mm});
            skLineSegment(sketch, "E49.0.2.29", {"start": v(6216.83, 2859.97) * mm, "end": v(6148.83, 2895.97) * mm});
            skLineSegment(sketch, "E49.0.2.30", {"start": v(6982.83, 2895.97) * mm, "end": v(6910.83, 2895.97) * mm});
            skLineSegment(sketch, "E49.0.2.31", {"start": v(6982.83, 2894.97) * mm, "end": v(6910.83, 2894.97) * mm});
            skLineSegment(sketch, "E49.0.2.32", {"start": v(6216.83, 2858.97) * mm, "end": v(6148.83, 2894.97) * mm});
            skLineSegment(sketch, "E49.0.2.33", {"start": v(6148.83, 2894.97) * mm, "end": v(6076.83, 2894.97) * mm});
            skLineSegment(sketch, "E49.0.2.34", {"start": v(6564.83, 2858.97) * mm, "end": v(6494.83, 2858.97) * mm});
            skLineSegment(sketch, "E49.0.2.35", {"start": v(6704.83, 2894.97) * mm, "end": v(6632.83, 2894.97) * mm});
            skLineSegment(sketch, "E49.0.2.36", {"start": v(7120.83, 2858.97) * mm, "end": v(7050.83, 2858.97) * mm});
            skLineSegment(sketch, "E49.0.2.37", {"start": v(6354.83, 2894.97) * mm, "end": v(6286.83, 2858.97) * mm});
            skLineSegment(sketch, "E49.0.2.38", {"start": v(6772.83, 2859.97) * mm, "end": v(6704.83, 2895.97) * mm});
            skLineSegment(sketch, "E49.0.2.39", {"start": v(6632.83, 2894.97) * mm, "end": v(6564.83, 2858.97) * mm});
            skLineSegment(sketch, "E49.0.2.40", {"start": v(6426.83, 2895.97) * mm, "end": v(6354.83, 2895.97) * mm});
            skLineSegment(sketch, "E49.0.2.41", {"start": v(6494.83, 2859.97) * mm, "end": v(6426.83, 2895.97) * mm});
            skLineSegment(sketch, "E49.0.2.42", {"start": v(6704.83, 2895.97) * mm, "end": v(6632.83, 2895.97) * mm});
            skLineSegment(sketch, "E49.0.2.43", {"start": v(7120.83, 2859.97) * mm, "end": v(7050.83, 2859.97) * mm});
            skLineSegment(sketch, "E49.0.2.44", {"start": v(6772.83, 2858.97) * mm, "end": v(6704.83, 2894.97) * mm});
            skLineSegment(sketch, "E49.0.2.45", {"start": v(7050.83, 2858.97) * mm, "end": v(6982.83, 2894.97) * mm});
            skLineSegment(sketch, "E49.0.2.46", {"start": v(7188.83, 2894.97) * mm, "end": v(7120.83, 2858.97) * mm});
            skLineSegment(sketch, "E49.0.2.47", {"start": v(6426.83, 2894.97) * mm, "end": v(6354.83, 2894.97) * mm});
            skLineSegment(sketch, "E49.0.2.48", {"start": v(6842.83, 2858.97) * mm, "end": v(6772.83, 2858.97) * mm});
            skLineSegment(sketch, "E49.0.2.49", {"start": v(6286.83, 2858.97) * mm, "end": v(6216.83, 2858.97) * mm});
            skLineSegment(sketch, "E49.0.2.50", {"start": v(6842.83, 2859.97) * mm, "end": v(6772.83, 2859.97) * mm});
            skLineSegment(sketch, "E49.0.2.51", {"start": v(7188.83, 2895.97) * mm, "end": v(7120.83, 2859.97) * mm});
            skLineSegment(sketch, "E49.0.2.52", {"start": v(7050.83, 2859.97) * mm, "end": v(6982.83, 2895.97) * mm});
            skLineSegment(sketch, "E49.0.2.53", {"start": v(6286.83, 2859.97) * mm, "end": v(6216.83, 2859.97) * mm});
            skLineSegment(sketch, "E49.0.2.54", {"start": v(6564.83, 2859.97) * mm, "end": v(6494.83, 2859.97) * mm});
            skLineSegment(sketch, "E49.0.2.55", {"start": v(6354.83, 2895.97) * mm, "end": v(6286.83, 2859.97) * mm});
            skLineSegment(sketch, "E49.0.2.56", {"start": v(6632.83, 2895.97) * mm, "end": v(6564.83, 2859.97) * mm});
            skLineSegment(sketch, "E49.0.2.57", {"start": v(6494.83, 2858.97) * mm, "end": v(6426.83, 2894.97) * mm});
            skLineSegment(sketch, "E49.0.3.0", {"start": v(5520.83, 2895.97) * mm, "end": v(5452.83, 2859.97) * mm});
            skLineSegment(sketch, "E49.0.3.1", {"start": v(5520.83, 2894.97) * mm, "end": v(5452.83, 2858.97) * mm});
            skLineSegment(sketch, "E49.0.3.2", {"start": v(5592.83, 2895.97) * mm, "end": v(5520.83, 2895.97) * mm});
            skLineSegment(sketch, "E49.0.3.3", {"start": v(5870.83, 2895.97) * mm, "end": v(5798.83, 2895.97) * mm});
            skLineSegment(sketch, "E49.0.3.4", {"start": v(5660.83, 2858.97) * mm, "end": v(5592.83, 2894.97) * mm});
            skLineSegment(sketch, "E49.0.3.5", {"start": v(5730.83, 2858.97) * mm, "end": v(5660.83, 2858.97) * mm});
            skLineSegment(sketch, "E49.0.3.6", {"start": v(5382.83, 2858.97) * mm, "end": v(5314.83, 2894.97) * mm});
            skLineSegment(sketch, "E49.0.3.7", {"start": v(5798.83, 2894.97) * mm, "end": v(5730.83, 2858.97) * mm});
            skLineSegment(sketch, "E49.0.3.8", {"start": v(5382.83, 2859.97) * mm, "end": v(5314.83, 2895.97) * mm});
            skLineSegment(sketch, "E49.0.3.9", {"start": v(5730.83, 2859.97) * mm, "end": v(5660.83, 2859.97) * mm});
            skLineSegment(sketch, "E49.0.3.10", {"start": v(6008.83, 2858.97) * mm, "end": v(5938.83, 2858.97) * mm});
            skLineSegment(sketch, "E49.0.3.11", {"start": v(5452.83, 2859.97) * mm, "end": v(5382.83, 2859.97) * mm});
            skLineSegment(sketch, "E49.0.3.12", {"start": v(5592.83, 2894.97) * mm, "end": v(5520.83, 2894.97) * mm});
            skLineSegment(sketch, "E49.0.3.13", {"start": v(5938.83, 2858.97) * mm, "end": v(5870.83, 2894.97) * mm});
            skLineSegment(sketch, "E49.0.3.14", {"start": v(5938.83, 2859.97) * mm, "end": v(5870.83, 2895.97) * mm});
            skLineSegment(sketch, "E49.0.3.15", {"start": v(5314.83, 2895.97) * mm, "end": v(5242.83, 2895.97) * mm});
            skLineSegment(sketch, "E49.0.3.16", {"start": v(5798.83, 2895.97) * mm, "end": v(5730.83, 2859.97) * mm});
            skLineSegment(sketch, "E49.0.3.17", {"start": v(6008.83, 2859.97) * mm, "end": v(5938.83, 2859.97) * mm});
            skLineSegment(sketch, "E49.0.3.18", {"start": v(5870.83, 2894.97) * mm, "end": v(5798.83, 2894.97) * mm});
            skLineSegment(sketch, "E49.0.3.19", {"start": v(5660.83, 2859.97) * mm, "end": v(5592.83, 2895.97) * mm});
            skLineSegment(sketch, "E49.0.3.20", {"start": v(5314.83, 2894.97) * mm, "end": v(5242.83, 2894.97) * mm});
            skLineSegment(sketch, "E49.0.3.21", {"start": v(5452.83, 2858.97) * mm, "end": v(5382.83, 2858.97) * mm});
            skLineSegment(sketch, "E49.0.3.22", {"start": v(4548.83, 2859.97) * mm, "end": v(4270.83, 2859.97) * mm, "construction": true});
            skLineSegment(sketch, "E49.0.3.23", {"start": v(4130.83, 2895.97) * mm, "end": v(4062.83, 2859.97) * mm});
            skLineSegment(sketch, "E49.0.3.24", {"start": v(4130.83, 2894.97) * mm, "end": v(4062.83, 2858.97) * mm});
            skLineSegment(sketch, "E49.0.3.25", {"start": v(4548.83, 2858.97) * mm, "end": v(4270.83, 2858.97) * mm, "construction": true});
            skLineSegment(sketch, "E49.0.3.26", {"start": v(4964.83, 2894.97) * mm, "end": v(4896.83, 2858.97) * mm});
            skLineSegment(sketch, "E49.0.3.27", {"start": v(4964.83, 2895.97) * mm, "end": v(4896.83, 2859.97) * mm});
            skLineSegment(sketch, "E49.0.3.28", {"start": v(4202.83, 2895.97) * mm, "end": v(4130.83, 2895.97) * mm});
            skLineSegment(sketch, "E49.0.3.29", {"start": v(4270.83, 2859.97) * mm, "end": v(4202.83, 2895.97) * mm});
            skLineSegment(sketch, "E49.0.3.30", {"start": v(5036.83, 2895.97) * mm, "end": v(4964.83, 2895.97) * mm});
            skLineSegment(sketch, "E49.0.3.31", {"start": v(5036.83, 2894.97) * mm, "end": v(4964.83, 2894.97) * mm});
            skLineSegment(sketch, "E49.0.3.32", {"start": v(4270.83, 2858.97) * mm, "end": v(4202.83, 2894.97) * mm});
            skLineSegment(sketch, "E49.0.3.33", {"start": v(4202.83, 2894.97) * mm, "end": v(4130.83, 2894.97) * mm});
            skLineSegment(sketch, "E49.0.3.34", {"start": v(4618.83, 2858.97) * mm, "end": v(4548.83, 2858.97) * mm});
            skLineSegment(sketch, "E49.0.3.35", {"start": v(4758.83, 2894.97) * mm, "end": v(4686.83, 2894.97) * mm});
            skLineSegment(sketch, "E49.0.3.36", {"start": v(5174.83, 2858.97) * mm, "end": v(5104.83, 2858.97) * mm});
            skLineSegment(sketch, "E49.0.3.37", {"start": v(4408.83, 2894.97) * mm, "end": v(4340.83, 2858.97) * mm});
            skLineSegment(sketch, "E49.0.3.38", {"start": v(4826.83, 2859.97) * mm, "end": v(4758.83, 2895.97) * mm});
            skLineSegment(sketch, "E49.0.3.39", {"start": v(4686.83, 2894.97) * mm, "end": v(4618.83, 2858.97) * mm});
            skLineSegment(sketch, "E49.0.3.40", {"start": v(4480.83, 2895.97) * mm, "end": v(4408.83, 2895.97) * mm});
            skLineSegment(sketch, "E49.0.3.41", {"start": v(4548.83, 2859.97) * mm, "end": v(4480.83, 2895.97) * mm});
            skLineSegment(sketch, "E49.0.3.42", {"start": v(4758.83, 2895.97) * mm, "end": v(4686.83, 2895.97) * mm});
            skLineSegment(sketch, "E49.0.3.43", {"start": v(5174.83, 2859.97) * mm, "end": v(5104.83, 2859.97) * mm});
            skLineSegment(sketch, "E49.0.3.44", {"start": v(4826.83, 2858.97) * mm, "end": v(4758.83, 2894.97) * mm});
            skLineSegment(sketch, "E49.0.3.45", {"start": v(5104.83, 2858.97) * mm, "end": v(5036.83, 2894.97) * mm});
            skLineSegment(sketch, "E49.0.3.46", {"start": v(5242.83, 2894.97) * mm, "end": v(5174.83, 2858.97) * mm});
            skLineSegment(sketch, "E49.0.3.47", {"start": v(4480.83, 2894.97) * mm, "end": v(4408.83, 2894.97) * mm});
            skLineSegment(sketch, "E49.0.3.48", {"start": v(4896.83, 2858.97) * mm, "end": v(4826.83, 2858.97) * mm});
            skLineSegment(sketch, "E49.0.3.49", {"start": v(4340.83, 2858.97) * mm, "end": v(4270.83, 2858.97) * mm});
            skLineSegment(sketch, "E49.0.3.50", {"start": v(4896.83, 2859.97) * mm, "end": v(4826.83, 2859.97) * mm});
            skLineSegment(sketch, "E49.0.3.51", {"start": v(5242.83, 2895.97) * mm, "end": v(5174.83, 2859.97) * mm});
            skLineSegment(sketch, "E49.0.3.52", {"start": v(5104.83, 2859.97) * mm, "end": v(5036.83, 2895.97) * mm});
            skLineSegment(sketch, "E49.0.3.53", {"start": v(4340.83, 2859.97) * mm, "end": v(4270.83, 2859.97) * mm});
            skLineSegment(sketch, "E49.0.3.54", {"start": v(4618.83, 2859.97) * mm, "end": v(4548.83, 2859.97) * mm});
            skLineSegment(sketch, "E49.0.3.55", {"start": v(4408.83, 2895.97) * mm, "end": v(4340.83, 2859.97) * mm});
            skLineSegment(sketch, "E49.0.3.56", {"start": v(4686.83, 2895.97) * mm, "end": v(4618.83, 2859.97) * mm});
            skLineSegment(sketch, "E49.0.3.57", {"start": v(4548.83, 2858.97) * mm, "end": v(4480.83, 2894.97) * mm});
            skLineSegment(sketch, "E49.0.4.0", {"start": v(3574.83, 2895.97) * mm, "end": v(3506.83, 2859.97) * mm});
            skLineSegment(sketch, "E49.0.4.1", {"start": v(3574.83, 2894.97) * mm, "end": v(3506.83, 2858.97) * mm});
            skLineSegment(sketch, "E49.0.4.2", {"start": v(3646.83, 2895.97) * mm, "end": v(3574.83, 2895.97) * mm});
            skLineSegment(sketch, "E49.0.4.3", {"start": v(3924.83, 2895.97) * mm, "end": v(3852.83, 2895.97) * mm});
            skLineSegment(sketch, "E49.0.4.4", {"start": v(3714.83, 2858.97) * mm, "end": v(3646.83, 2894.97) * mm});
            skLineSegment(sketch, "E49.0.4.5", {"start": v(3784.83, 2858.97) * mm, "end": v(3714.83, 2858.97) * mm});
            skLineSegment(sketch, "E49.0.4.6", {"start": v(3436.83, 2858.97) * mm, "end": v(3368.83, 2894.97) * mm});
            skLineSegment(sketch, "E49.0.4.7", {"start": v(3852.83, 2894.97) * mm, "end": v(3784.83, 2858.97) * mm});
            skLineSegment(sketch, "E49.0.4.8", {"start": v(3436.83, 2859.97) * mm, "end": v(3368.83, 2895.97) * mm});
            skLineSegment(sketch, "E49.0.4.9", {"start": v(3784.83, 2859.97) * mm, "end": v(3714.83, 2859.97) * mm});
            skLineSegment(sketch, "E49.0.4.10", {"start": v(4062.83, 2858.97) * mm, "end": v(3992.83, 2858.97) * mm});
            skLineSegment(sketch, "E49.0.4.11", {"start": v(3506.83, 2859.97) * mm, "end": v(3436.83, 2859.97) * mm});
            skLineSegment(sketch, "E49.0.4.12", {"start": v(3646.83, 2894.97) * mm, "end": v(3574.83, 2894.97) * mm});
            skLineSegment(sketch, "E49.0.4.13", {"start": v(3992.83, 2858.97) * mm, "end": v(3924.83, 2894.97) * mm});
            skLineSegment(sketch, "E49.0.4.14", {"start": v(3992.83, 2859.97) * mm, "end": v(3924.83, 2895.97) * mm});
            skLineSegment(sketch, "E49.0.4.15", {"start": v(3368.83, 2895.97) * mm, "end": v(3296.83, 2895.97) * mm});
            skLineSegment(sketch, "E49.0.4.16", {"start": v(3852.83, 2895.97) * mm, "end": v(3784.83, 2859.97) * mm});
            skLineSegment(sketch, "E49.0.4.17", {"start": v(4062.83, 2859.97) * mm, "end": v(3992.83, 2859.97) * mm});
            skLineSegment(sketch, "E49.0.4.18", {"start": v(3924.83, 2894.97) * mm, "end": v(3852.83, 2894.97) * mm});
            skLineSegment(sketch, "E49.0.4.19", {"start": v(3714.83, 2859.97) * mm, "end": v(3646.83, 2895.97) * mm});
            skLineSegment(sketch, "E49.0.4.20", {"start": v(3368.83, 2894.97) * mm, "end": v(3296.83, 2894.97) * mm});
            skLineSegment(sketch, "E49.0.4.21", {"start": v(3506.83, 2858.97) * mm, "end": v(3436.83, 2858.97) * mm});
            skLineSegment(sketch, "E49.0.4.22", {"start": v(2602.83, 2859.97) * mm, "end": v(2324.83, 2859.97) * mm, "construction": true});
            skLineSegment(sketch, "E49.0.4.23", {"start": v(2184.83, 2895.97) * mm, "end": v(2116.83, 2859.97) * mm});
            skLineSegment(sketch, "E49.0.4.24", {"start": v(2184.83, 2894.97) * mm, "end": v(2116.83, 2858.97) * mm});
            skLineSegment(sketch, "E49.0.4.25", {"start": v(2602.83, 2858.97) * mm, "end": v(2324.83, 2858.97) * mm, "construction": true});
            skLineSegment(sketch, "E49.0.4.26", {"start": v(3018.83, 2894.97) * mm, "end": v(2950.83, 2858.97) * mm});
            skLineSegment(sketch, "E49.0.4.27", {"start": v(3018.83, 2895.97) * mm, "end": v(2950.83, 2859.97) * mm});
            skLineSegment(sketch, "E49.0.4.28", {"start": v(2256.83, 2895.97) * mm, "end": v(2184.83, 2895.97) * mm});
            skLineSegment(sketch, "E49.0.4.29", {"start": v(2324.83, 2859.97) * mm, "end": v(2256.83, 2895.97) * mm});
            skLineSegment(sketch, "E49.0.4.30", {"start": v(3090.83, 2895.97) * mm, "end": v(3018.83, 2895.97) * mm});
            skLineSegment(sketch, "E49.0.4.31", {"start": v(3090.83, 2894.97) * mm, "end": v(3018.83, 2894.97) * mm});
            skLineSegment(sketch, "E49.0.4.32", {"start": v(2324.83, 2858.97) * mm, "end": v(2256.83, 2894.97) * mm});
            skLineSegment(sketch, "E49.0.4.33", {"start": v(2256.83, 2894.97) * mm, "end": v(2184.83, 2894.97) * mm});
            skLineSegment(sketch, "E49.0.4.34", {"start": v(2672.83, 2858.97) * mm, "end": v(2602.83, 2858.97) * mm});
            skLineSegment(sketch, "E49.0.4.35", {"start": v(2812.83, 2894.97) * mm, "end": v(2740.83, 2894.97) * mm});
            skLineSegment(sketch, "E49.0.4.36", {"start": v(3228.83, 2858.97) * mm, "end": v(3158.83, 2858.97) * mm});
            skLineSegment(sketch, "E49.0.4.37", {"start": v(2462.83, 2894.97) * mm, "end": v(2394.83, 2858.97) * mm});
            skLineSegment(sketch, "E49.0.4.38", {"start": v(2880.83, 2859.97) * mm, "end": v(2812.83, 2895.97) * mm});
            skLineSegment(sketch, "E49.0.4.39", {"start": v(2740.83, 2894.97) * mm, "end": v(2672.83, 2858.97) * mm});
            skLineSegment(sketch, "E49.0.4.40", {"start": v(2534.83, 2895.97) * mm, "end": v(2462.83, 2895.97) * mm});
            skLineSegment(sketch, "E49.0.4.41", {"start": v(2602.83, 2859.97) * mm, "end": v(2534.83, 2895.97) * mm});
            skLineSegment(sketch, "E49.0.4.42", {"start": v(2812.83, 2895.97) * mm, "end": v(2740.83, 2895.97) * mm});
            skLineSegment(sketch, "E49.0.4.43", {"start": v(3228.83, 2859.97) * mm, "end": v(3158.83, 2859.97) * mm});
            skLineSegment(sketch, "E49.0.4.44", {"start": v(2880.83, 2858.97) * mm, "end": v(2812.83, 2894.97) * mm});
            skLineSegment(sketch, "E49.0.4.45", {"start": v(3158.83, 2858.97) * mm, "end": v(3090.83, 2894.97) * mm});
            skLineSegment(sketch, "E49.0.4.46", {"start": v(3296.83, 2894.97) * mm, "end": v(3228.83, 2858.97) * mm});
            skLineSegment(sketch, "E49.0.4.47", {"start": v(2534.83, 2894.97) * mm, "end": v(2462.83, 2894.97) * mm});
            skLineSegment(sketch, "E49.0.4.48", {"start": v(2950.83, 2858.97) * mm, "end": v(2880.83, 2858.97) * mm});
            skLineSegment(sketch, "E49.0.4.49", {"start": v(2394.83, 2858.97) * mm, "end": v(2324.83, 2858.97) * mm});
            skLineSegment(sketch, "E49.0.4.50", {"start": v(2950.83, 2859.97) * mm, "end": v(2880.83, 2859.97) * mm});
            skLineSegment(sketch, "E49.0.4.51", {"start": v(3296.83, 2895.97) * mm, "end": v(3228.83, 2859.97) * mm});
            skLineSegment(sketch, "E49.0.4.52", {"start": v(3158.83, 2859.97) * mm, "end": v(3090.83, 2895.97) * mm});
            skLineSegment(sketch, "E49.0.4.53", {"start": v(2394.83, 2859.97) * mm, "end": v(2324.83, 2859.97) * mm});
            skLineSegment(sketch, "E49.0.4.54", {"start": v(2672.83, 2859.97) * mm, "end": v(2602.83, 2859.97) * mm});
            skLineSegment(sketch, "E49.0.4.55", {"start": v(2462.83, 2895.97) * mm, "end": v(2394.83, 2859.97) * mm});
            skLineSegment(sketch, "E49.0.4.56", {"start": v(2740.83, 2895.97) * mm, "end": v(2672.83, 2859.97) * mm});
            skLineSegment(sketch, "E49.0.4.57", {"start": v(2602.83, 2858.97) * mm, "end": v(2534.83, 2894.97) * mm});
            skLineSegment(sketch, "E49.0.5.0", {"start": v(1628.83, 2895.97) * mm, "end": v(1560.83, 2859.97) * mm});
            skLineSegment(sketch, "E49.0.5.1", {"start": v(1628.83, 2894.97) * mm, "end": v(1560.83, 2858.97) * mm});
            skLineSegment(sketch, "E49.0.5.2", {"start": v(1700.83, 2895.97) * mm, "end": v(1628.83, 2895.97) * mm});
            skLineSegment(sketch, "E49.0.5.3", {"start": v(1978.83, 2895.97) * mm, "end": v(1906.83, 2895.97) * mm});
            skLineSegment(sketch, "E49.0.5.4", {"start": v(1768.83, 2858.97) * mm, "end": v(1700.83, 2894.97) * mm});
            skLineSegment(sketch, "E49.0.5.5", {"start": v(1838.83, 2858.97) * mm, "end": v(1768.83, 2858.97) * mm});
            skLineSegment(sketch, "E49.0.5.6", {"start": v(1490.83, 2858.97) * mm, "end": v(1422.83, 2894.97) * mm});
            skLineSegment(sketch, "E49.0.5.7", {"start": v(1906.83, 2894.97) * mm, "end": v(1838.83, 2858.97) * mm});
            skLineSegment(sketch, "E49.0.5.8", {"start": v(1490.83, 2859.97) * mm, "end": v(1422.83, 2895.97) * mm});
            skLineSegment(sketch, "E49.0.5.9", {"start": v(1838.83, 2859.97) * mm, "end": v(1768.83, 2859.97) * mm});
            skLineSegment(sketch, "E49.0.5.10", {"start": v(2116.83, 2858.97) * mm, "end": v(2046.83, 2858.97) * mm});
            skLineSegment(sketch, "E49.0.5.11", {"start": v(1560.83, 2859.97) * mm, "end": v(1490.83, 2859.97) * mm});
            skLineSegment(sketch, "E49.0.5.12", {"start": v(1700.83, 2894.97) * mm, "end": v(1628.83, 2894.97) * mm});
            skLineSegment(sketch, "E49.0.5.13", {"start": v(2046.83, 2858.97) * mm, "end": v(1978.83, 2894.97) * mm});
            skLineSegment(sketch, "E49.0.5.14", {"start": v(2046.83, 2859.97) * mm, "end": v(1978.83, 2895.97) * mm});
            skLineSegment(sketch, "E49.0.5.15", {"start": v(1422.83, 2895.97) * mm, "end": v(1350.83, 2895.97) * mm});
            skLineSegment(sketch, "E49.0.5.16", {"start": v(1906.83, 2895.97) * mm, "end": v(1838.83, 2859.97) * mm});
            skLineSegment(sketch, "E49.0.5.17", {"start": v(2116.83, 2859.97) * mm, "end": v(2046.83, 2859.97) * mm});
            skLineSegment(sketch, "E49.0.5.18", {"start": v(1978.83, 2894.97) * mm, "end": v(1906.83, 2894.97) * mm});
            skLineSegment(sketch, "E49.0.5.19", {"start": v(1768.83, 2859.97) * mm, "end": v(1700.83, 2895.97) * mm});
            skLineSegment(sketch, "E49.0.5.20", {"start": v(1422.83, 2894.97) * mm, "end": v(1350.83, 2894.97) * mm});
            skLineSegment(sketch, "E49.0.5.21", {"start": v(1560.83, 2858.97) * mm, "end": v(1490.83, 2858.97) * mm});
            skLineSegment(sketch, "E49.0.5.22", {"start": v(656.83, 2859.97) * mm, "end": v(378.83, 2859.97) * mm, "construction": true});
            skLineSegment(sketch, "E49.0.5.23", {"start": v(238.83, 2895.97) * mm, "end": v(170.83, 2859.97) * mm});
            skLineSegment(sketch, "E49.0.5.24", {"start": v(238.83, 2894.97) * mm, "end": v(170.83, 2858.97) * mm});
            skLineSegment(sketch, "E49.0.5.25", {"start": v(656.83, 2858.97) * mm, "end": v(378.83, 2858.97) * mm, "construction": true});
            skLineSegment(sketch, "E49.0.5.26", {"start": v(1072.83, 2894.97) * mm, "end": v(1004.83, 2858.97) * mm});
            skLineSegment(sketch, "E49.0.5.27", {"start": v(1072.83, 2895.97) * mm, "end": v(1004.83, 2859.97) * mm});
            skLineSegment(sketch, "E49.0.5.28", {"start": v(310.83, 2895.97) * mm, "end": v(238.83, 2895.97) * mm});
            skLineSegment(sketch, "E49.0.5.29", {"start": v(378.83, 2859.97) * mm, "end": v(310.83, 2895.97) * mm});
            skLineSegment(sketch, "E49.0.5.30", {"start": v(1144.83, 2895.97) * mm, "end": v(1072.83, 2895.97) * mm});
            skLineSegment(sketch, "E49.0.5.31", {"start": v(1144.83, 2894.97) * mm, "end": v(1072.83, 2894.97) * mm});
            skLineSegment(sketch, "E49.0.5.32", {"start": v(378.83, 2858.97) * mm, "end": v(310.83, 2894.97) * mm});
            skLineSegment(sketch, "E49.0.5.33", {"start": v(310.83, 2894.97) * mm, "end": v(238.83, 2894.97) * mm});
            skLineSegment(sketch, "E49.0.5.34", {"start": v(726.83, 2858.97) * mm, "end": v(656.83, 2858.97) * mm});
            skLineSegment(sketch, "E49.0.5.35", {"start": v(866.83, 2894.97) * mm, "end": v(794.83, 2894.97) * mm});
            skLineSegment(sketch, "E49.0.5.36", {"start": v(1282.83, 2858.97) * mm, "end": v(1212.83, 2858.97) * mm});
            skLineSegment(sketch, "E49.0.5.37", {"start": v(516.83, 2894.97) * mm, "end": v(448.83, 2858.97) * mm});
            skLineSegment(sketch, "E49.0.5.38", {"start": v(934.83, 2859.97) * mm, "end": v(866.83, 2895.97) * mm});
            skLineSegment(sketch, "E49.0.5.39", {"start": v(794.83, 2894.97) * mm, "end": v(726.83, 2858.97) * mm});
            skLineSegment(sketch, "E49.0.5.40", {"start": v(588.83, 2895.97) * mm, "end": v(516.83, 2895.97) * mm});
            skLineSegment(sketch, "E49.0.5.41", {"start": v(656.83, 2859.97) * mm, "end": v(588.83, 2895.97) * mm});
            skLineSegment(sketch, "E49.0.5.42", {"start": v(866.83, 2895.97) * mm, "end": v(794.83, 2895.97) * mm});
            skLineSegment(sketch, "E49.0.5.43", {"start": v(1282.83, 2859.97) * mm, "end": v(1212.83, 2859.97) * mm});
            skLineSegment(sketch, "E49.0.5.44", {"start": v(934.83, 2858.97) * mm, "end": v(866.83, 2894.97) * mm});
            skLineSegment(sketch, "E49.0.5.45", {"start": v(1212.83, 2858.97) * mm, "end": v(1144.83, 2894.97) * mm});
            skLineSegment(sketch, "E49.0.5.46", {"start": v(1350.83, 2894.97) * mm, "end": v(1282.83, 2858.97) * mm});
            skLineSegment(sketch, "E49.0.5.47", {"start": v(588.83, 2894.97) * mm, "end": v(516.83, 2894.97) * mm});
            skLineSegment(sketch, "E49.0.5.48", {"start": v(1004.83, 2858.97) * mm, "end": v(934.83, 2858.97) * mm});
            skLineSegment(sketch, "E49.0.5.49", {"start": v(448.83, 2858.97) * mm, "end": v(378.83, 2858.97) * mm});
            skLineSegment(sketch, "E49.0.5.50", {"start": v(1004.83, 2859.97) * mm, "end": v(934.83, 2859.97) * mm});
            skLineSegment(sketch, "E49.0.5.51", {"start": v(1350.83, 2895.97) * mm, "end": v(1282.83, 2859.97) * mm});
            skLineSegment(sketch, "E49.0.5.52", {"start": v(1212.83, 2859.97) * mm, "end": v(1144.83, 2895.97) * mm});
            skLineSegment(sketch, "E49.0.5.53", {"start": v(448.83, 2859.97) * mm, "end": v(378.83, 2859.97) * mm});
            skLineSegment(sketch, "E49.0.5.54", {"start": v(726.83, 2859.97) * mm, "end": v(656.83, 2859.97) * mm});
            skLineSegment(sketch, "E49.0.5.55", {"start": v(516.83, 2895.97) * mm, "end": v(448.83, 2859.97) * mm});
            skLineSegment(sketch, "E49.0.5.56", {"start": v(794.83, 2895.97) * mm, "end": v(726.83, 2859.97) * mm});
            skLineSegment(sketch, "E49.0.5.57", {"start": v(656.83, 2858.97) * mm, "end": v(588.83, 2894.97) * mm});
            skLineSegment(sketch, "E49.direction1", {"start": v(11846.83, 2858.97) * mm, "end": v(11846.83, 2883.97) * mm, "construction": true});
            skLineSegment(sketch, "E49.direction2", {"start": v(11846.83, 2858.97) * mm, "end": v(9900.83, 2858.97) * mm, "construction": true});
            skLineSegment(sketch, "E50", {"start": v(170.83, 2859.97) * mm, "end": v(100, 2859.97) * mm});
            skLineSegment(sketch, "E51", {"start": v(100, 2859.97) * mm, "end": v(100, 2858.97) * mm});
            skLineSegment(sketch, "E52", {"start": v(100, 2858.97) * mm, "end": v(170.83, 2858.97) * mm});
            skSolve(sketch);
        }
        {
            var Q0;
            Q0=qSketchRegion(id+"F12",true);
            extrude(context, id + "F13", {"entities" : qUnion([Q0]), "operationType" : NewBodyOperationType.ADD, "depth" : 2236 * mm, "offsetDistance" : 25 * mm});
        }
    });
